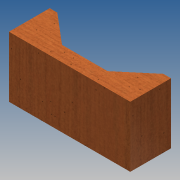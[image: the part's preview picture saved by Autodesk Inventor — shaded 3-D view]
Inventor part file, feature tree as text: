
AUTODESK INVENTOR PART (.ipt)
format: ipt  version: 2013 SP2 (Build 170200200, 200)  size: 99,328 bytes
history: native  units: in
note: dims shown in document units (in); Inventor stores cm internally (conversion verified against a paired STEP export)
features: extrude x1, sketch x1
ambient origin geometry x8: Origin, YZ Plane, XZ Plane, XY Plane, X Axis, Y Axis, Z Axis, Center Point
bodies: Solid1 (feature_tree)
feature tree (2):
  extrude  "Extrusion1"  Depth=8.0in
  sketch  "Sketch1"  dims[d4=8.0in d5=8.0in d6=5.0in d7=1.5in d8=4.0in d9=0.0in]
